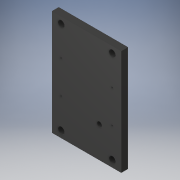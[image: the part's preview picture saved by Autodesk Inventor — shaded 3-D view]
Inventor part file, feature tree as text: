
AUTODESK INVENTOR PART (.ipt)
format: ipt  version: 2017 (Build 210142000, 142)  size: 195,584 bytes
history: native  units: in
note: dims shown in document units (in); Inventor stores cm internally (conversion verified against a paired STEP export)
features: sketch x5, extrude x5
ambient origin geometry x8: Origin, YZ Plane, XZ Plane, XY Plane, X Axis, Y Axis, Z Axis, Center Point
bodies: Body1 (feature_tree)
feature tree (10):
  sketch  "Sketch1"  dims[d0=1.9375in d1=1.25in]
  extrude  "Extrusion2"  Depth=1.25in
  extrude  "Extrusion3"  Depth=1.25in
  extrude  "Extrusion4"  Depth=0.25in
  extrude  "Extrusion5"  Depth=2.125in
  extrude  "Extrusion6"  Depth=0.25in
  sketch  "Sketch7"  dims[d11=0.25in d12=0.25in]
  sketch  "Sketch8"  dims[d13=2.5in d14=2.125in]
  sketch  "Sketch9"  dims[d25=1.45in d26=1.45in d27=0.0625in d28=1.125in d29=1.125in d30=0.25in d31=0.25in d32=2.625in d33=4.0in d34=1.9375in d35=1.25in d36=0.0625in d37=1.9375in d38=1.25in d39=0.25in d40=0.25in d41=2.5in d42=2.125in d43=1.45in d44=1.45in d45=0.0625in d46=1.125in d47=1.125in d48=0.25in d49=0.25in d50=2.625in d51=4.0in d114=0.25in d115=0.0in d116=0.25in d117=0.0in d118=0.1875in d119=0.1875in d120=0.1875in d121=0.0625in d122=0.0in d123=0.1875in d124=0.125in d125=0.0in d126=0.25in d127=0.25in d128=0.25in d129=0.0in]
  sketch  "Sketch3"  dims[d2=0.0625in d3=0.7874in d5=1.9375in d6=0.7874in d8=1.25in]
